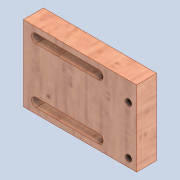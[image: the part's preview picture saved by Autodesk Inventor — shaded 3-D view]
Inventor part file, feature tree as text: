
AUTODESK INVENTOR PART (.ipt)
format: ipt  version: 2020 (Build 240168000, 168)  size: 199,168 bytes
history: native  units: mm
features: sketch x3, other x3, extrude x2, reference x2, hole x1
ambient origin geometry x8: Origin, YZ Plane, XZ Plane, XY Plane, X Axis, Y Axis, Z Axis, Center Point
bodies: Solid1 (feature_tree)
feature tree (11):
  extrude  "Extrusion1"  Depth=30.0mm
  extrude  "Extrusion5"  Depth=3.5mm
  hole  "Hole1"  [1 undecoded]
  sketch  "Sketch1"  dims[d0=45.0mm d1=30.0mm]
  sketch  "Sketch5"  dims[d2=8.0mm d3=0.0mm d29=3.5mm]
  sketch  "Sketch6"  dims[d30=4.0mm d31=4.0mm d33=25.0mm d34=10.0mm d35=0.0mm d36=5.0mm d37=2.459mm d38=8.0mm d39=4.0mm d40=2.0mm d41=90.0deg d42=8.0mm d43=20.594885mm]
  reference  "Reference1"
  reference  "Reference2"
  parser-record x1  (decoder bookkeeping rows leaked as tree rows — omitted from the tree; the rows remain in map.json)
  other  "0005-00-00 Ansamblu_General_V1.iam"
  other  "0005-20-1003 Switch:2"
note: 1 required parameter value undecoded (feature->parameter linkage not recoverable at this tier; creation-order binding heuristic only, values carry confidence <= 0.55)
note: 1 file-system path scrubbed to <path> (originals preserved in map.json)
